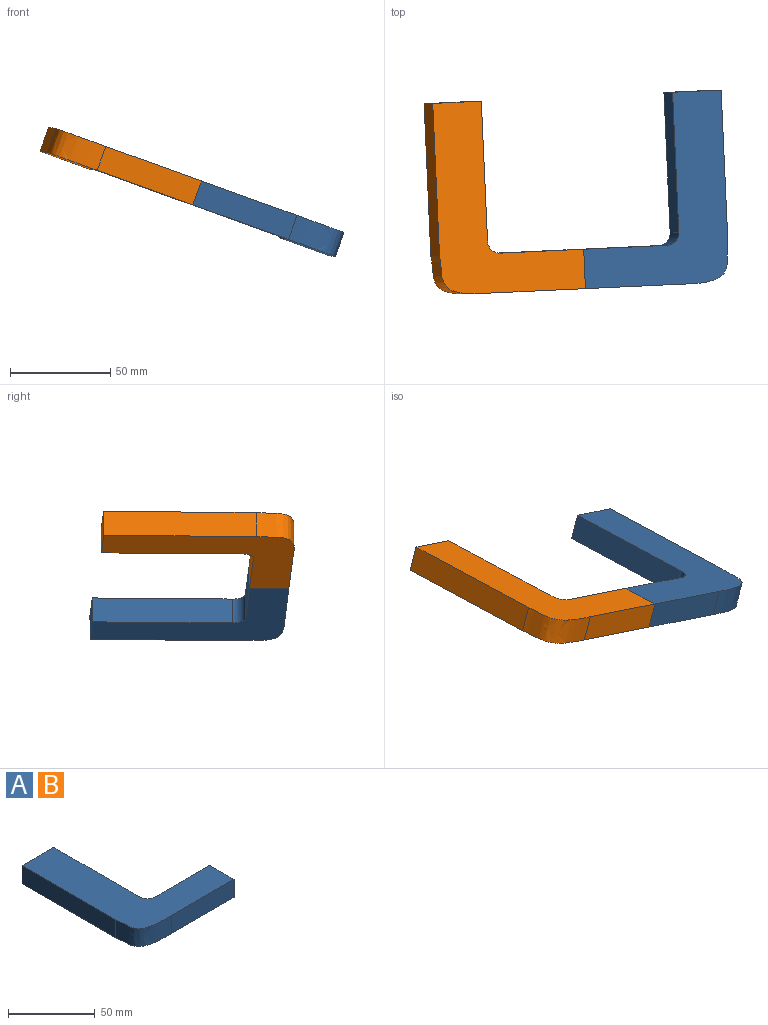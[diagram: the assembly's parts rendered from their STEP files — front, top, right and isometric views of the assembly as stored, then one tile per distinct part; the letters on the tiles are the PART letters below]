
ASSEMBLY  parts=2 mates=1
PART A: 10 faces, bbox 80.5x96.9x12.7 mm
  f0: extruded ~25.8x19.76mm, area 505.3mm2, adj f1,f7,f8,f9
  f1: plane 50.8x12.7mm, normal (0,-1,0), area 645.2mm2, adj f0,f2,f8,f9
  f2: plane 19.68x12.7mm, normal (1,0,0), area 250mm2, adj f1,f3,f8,f9
  f3: plane 44.45x12.7mm, normal (0,1,0), area 564.5mm2, adj f2,f4,f8,f9
  f4: cylinder r=6.35mm len=12.7mm, axis (0,0,-1), area 126.7mm2, adj f3,f5,f8,f9
  f5: plane 69.85x12.7mm, normal (1,0,0), area 887.1mm2, adj f4,f6,f8,f9
  f6: plane 25.8x12.7mm, normal (0,1,0), area 327.6mm2, adj f5,f7,f8,f9
  f7: plane 76.2x12.7mm, normal (-1,0,0), area 967.7mm2, adj f0,f6,f8,f9
  f8: plane 96.95x80.54mm, normal (0,0,1), area 3439.7mm2, adj f0,f1,f2,f3,f4,f5,f6,f7
  f9: plane 96.95x80.54mm, normal (0,0,-1), area 3439.7mm2, adj f0,f1,f2,f3,f4,f5,f6,f7
PART B: same geometry as A
PLACE A rot(axis=(0.02,-1,0),160.2deg) t=(43.7,7.61,4.88)mm
PLACE B rot(axis=(0,0.99,0.13),20deg) t=(-56.08,3,27.39)mm
MATE parallel A.f2 <-> B.f2  axis (-0.94,-0.04,0.34) through (-5.75,-4.53,16.06)mm
